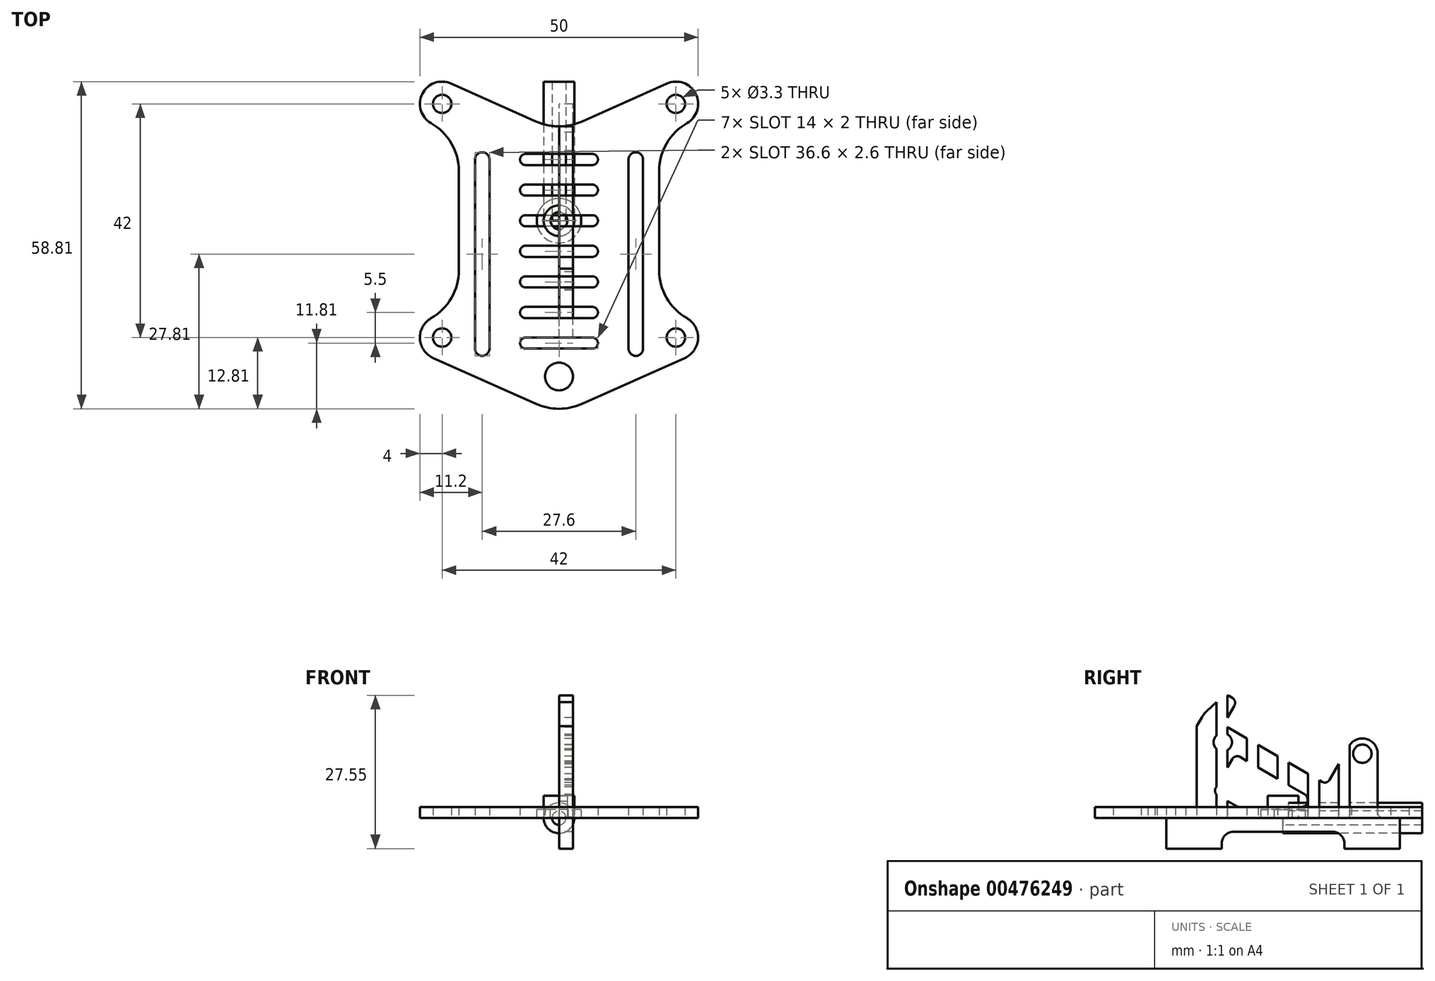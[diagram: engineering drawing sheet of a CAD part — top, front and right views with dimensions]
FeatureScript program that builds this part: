
annotation { "Feature Type Name" : "Feature", "Feature Type Description" : "" }
export const myFeature = defineFeature(function(context is Context, id is Id, definition is map)
    precondition{}
    {
        {
            var Q0;
            Q0=qCreatedBy(makeId("Right.planeOp"),FACE);
            var sketch = newSketch(context, id + "F0", { "sketchPlane" : qUnion([Q0])});
            skLineSegment(sketch, "E0.bottom", {"start": v(-21, 0) * mm, "end": v(-18, 0) * mm});
            skLineSegment(sketch, "E0.top", {"start": v(-21, -5.5) * mm, "end": v(-11, -5.5) * mm});
            skLineSegment(sketch, "E0.left", {"start": v(-21, 0) * mm, "end": v(-21, -5.5) * mm});
            skLineSegment(sketch, "E0.right", {"start": v(21, 0) * mm, "end": v(21, -5.5) * mm});
            skLineSegment(sketch, "E1.bottom", {"start": v(-9.89, 16.25) * mm, "end": v(7, 6.5) * mm});
            skLineSegment(sketch, "E1.left", {"start": v(-10.25, 17.62) * mm, "end": v(-8.75, 20.21) * mm});
            skPoint(sketch, "E1.middle", {"position": v(-0.2, 13.54) * mm});
            skLineSegment(sketch, "E2", {"start": v(8.37, 6.87) * mm, "end": v(11.87, 12.93) * mm});
            skLineSegment(sketch, "E3", {"start": v(17, 11.55) * mm, "end": v(17, 1) * mm});
            skLineSegment(sketch, "E4", {"start": v(-9.12, 21.58) * mm, "end": v(-9.77, 21.96) * mm});
            skLineSegment(sketch, "E5", {"start": v(-10.96, 21.82) * mm, "end": v(-13.68, 19.25) * mm});
            skLineSegment(sketch, "E6", {"start": v(-14.58, 18.11) * mm, "end": v(-16.33, 15.09) * mm});
            skLineSegment(sketch, "E7", {"start": v(-17, 12.59) * mm, "end": v(-17, 1) * mm});
            skArc(sketch, "E8", {"start": v(17, 11.55) * mm, "mid": v(14.96, 14.2) * mm, "end": v(11.87, 12.93) * mm});
            skLineSegment(sketch, "E9", {"start": v(-7.74, 10.97) * mm, "end": v(3.89, 4.26) * mm});
            skLineSegment(sketch, "E10", {"start": v(-7.94, 2) * mm, "end": v(3.39, 2) * mm});
            skLineSegment(sketch, "E11", {"start": v(-8.44, 2.13) * mm, "end": v(-11.74, 4.04) * mm});
            skLineSegment(sketch, "E12", {"start": v(-12.1, 5.4) * mm, "end": v(-9.1, 10.6) * mm});
            skLineSegment(sketch, "E13", {"start": v(4.39, 3.4) * mm, "end": v(4.39, 3) * mm});
            skLineSegment(sketch, "E14.trimOffspring", {"start": v(18, 0) * mm, "end": v(21, 0) * mm});
            skCircle(sketch, "E15", {"center": v(-10.83, 13.62) * mm, "radius": 1.65 * mm});
            skCircle(sketch, "E16", {"center": v(-10.83, 13.62) * mm, "radius": 2.75 * mm, "construction": true});
            skPoint(sketch, "E17.visualSharp", {"position": v(-8.6, 11.47) * mm});
            skArc(sketch, "E17.filletArc", {"start": v(-7.74, 10.97) * mm, "mid": v(-8.5, 11.07) * mm, "end": v(-9.1, 10.6) * mm});
            skPoint(sketch, "E18.visualSharp", {"position": v(4.39, 3.97) * mm});
            skArc(sketch, "E18.filletArc", {"start": v(4.39, 3.4) * mm, "mid": v(4.25, 3.9) * mm, "end": v(3.89, 4.26) * mm});
            skPoint(sketch, "E19.visualSharp", {"position": v(4.39, 2) * mm});
            skArc(sketch, "E19.filletArc", {"start": v(3.39, 2) * mm, "mid": v(4.1, 2.3) * mm, "end": v(4.39, 3) * mm});
            skPoint(sketch, "E20.visualSharp", {"position": v(-8.2, 2) * mm});
            skArc(sketch, "E20.filletArc", {"start": v(-8.44, 2.13) * mm, "mid": v(-8.2, 2.03) * mm, "end": v(-7.94, 2) * mm});
            skPoint(sketch, "E21.visualSharp", {"position": v(-12.6, 4.54) * mm});
            skArc(sketch, "E21.filletArc", {"start": v(-12.1, 5.4) * mm, "mid": v(-12.2, 4.65) * mm, "end": v(-11.74, 4.04) * mm});
            skPoint(sketch, "E22.visualSharp", {"position": v(17, 0) * mm});
            skArc(sketch, "E22.filletArc", {"start": v(17, 1) * mm, "mid": v(17.3, 0.3) * mm, "end": v(18, 0) * mm});
            skPoint(sketch, "E23.visualSharp", {"position": v(-17, 0) * mm});
            skArc(sketch, "E23.filletArc", {"start": v(-18, 0) * mm, "mid": v(-17.3, 0.3) * mm, "end": v(-17, 1) * mm});
            skPoint(sketch, "E24.visualSharp", {"position": v(-17, 13.93) * mm});
            skArc(sketch, "E24.filletArc", {"start": v(-16.33, 15.09) * mm, "mid": v(-16.83, 13.88) * mm, "end": v(-17, 12.59) * mm});
            skPoint(sketch, "E25.visualSharp", {"position": v(-14.22, 18.75) * mm});
            skArc(sketch, "E25.filletArc", {"start": v(-13.68, 19.25) * mm, "mid": v(-14.17, 18.72) * mm, "end": v(-14.58, 18.11) * mm});
            skPoint(sketch, "E26.visualSharp", {"position": v(-10.42, 22.33) * mm});
            skArc(sketch, "E26.filletArc", {"start": v(-9.77, 21.96) * mm, "mid": v(-10.39, 22.09) * mm, "end": v(-10.96, 21.82) * mm});
            skPoint(sketch, "E27.visualSharp", {"position": v(-8.25, 21.08) * mm});
            skArc(sketch, "E27.filletArc", {"start": v(-8.75, 20.21) * mm, "mid": v(-8.65, 20.97) * mm, "end": v(-9.12, 21.58) * mm});
            skPoint(sketch, "E28.visualSharp", {"position": v(-10.75, 16.75) * mm});
            skArc(sketch, "E28.filletArc", {"start": v(-10.25, 17.62) * mm, "mid": v(-10.35, 16.86) * mm, "end": v(-9.89, 16.25) * mm});
            skPoint(sketch, "E29.visualSharp", {"position": v(7.87, 6) * mm});
            skArc(sketch, "E29.filletArc", {"start": v(7, 6.5) * mm, "mid": v(7.76, 6.4) * mm, "end": v(8.37, 6.87) * mm});
            skCircle(sketch, "E30", {"center": v(14.25, 11.55) * mm, "radius": 1.65 * mm});
            skLineSegment(sketch, "E31", {"start": v(-11, -5.5) * mm, "end": v(-11, -4.5) * mm});
            skLineSegment(sketch, "E32", {"start": v(-9, -2.5) * mm, "end": v(9, -2.5) * mm});
            skLineSegment(sketch, "E33", {"start": v(11, -4.5) * mm, "end": v(11, -5.5) * mm});
            skLineSegment(sketch, "E34.trimOffspring", {"start": v(11, -5.5) * mm, "end": v(21, -5.5) * mm});
            skPoint(sketch, "E35.visualSharp", {"position": v(-11, -2.5) * mm});
            skArc(sketch, "E35.filletArc", {"start": v(-9, -2.5) * mm, "mid": v(-10.41, -3.09) * mm, "end": v(-11, -4.5) * mm});
            skPoint(sketch, "E36.visualSharp", {"position": v(11, -2.5) * mm});
            skArc(sketch, "E36.filletArc", {"start": v(11, -4.5) * mm, "mid": v(10.41, -3.09) * mm, "end": v(9, -2.5) * mm});
            skSolve(sketch);
        }
        {
            var Q0;
            Q0=makeQuery(id+"F0.imprint","IMPRINT",FACE,{"disambiguationData":[TD([[makeQuery(id+"F0.imprint","IMPRINT",EDGE,{"derivedFrom":sQuery(id+"F0.wireOp",EDGE,"E0.bottom")}),-1.0]])]});
            extrude(context, id + "F1", {"entities" : qUnion([Q0]), "depth" : 2.5 * mm, "offsetDistance" : 25 * mm});
        }
        {
            var Q0;
            Q0=qCreatedBy(makeId("Top.planeOp"),FACE);
            var sketch = newSketch(context, id + "F2", { "sketchPlane" : qUnion([Q0])});
            skCircle(sketch, "E37", {"center": v(-21, 21) * mm, "radius": 1.65 * mm});
            skCircle(sketch, "E38.MirrorC", {"center": v(21, 21) * mm, "radius": 1.65 * mm});
            skCircle(sketch, "E39.MirrorC", {"center": v(-21, -21) * mm, "radius": 1.65 * mm});
            skCircle(sketch, "E40.MirrorC", {"center": v(21, -21) * mm, "radius": 1.65 * mm});
            skArc(sketch, "E41", {"start": v(-19.37, 24.65) * mm, "mid": v(-24.56, 22.82) * mm, "end": v(-23, 17.54) * mm});
            skArc(sketch, "E42", {"start": v(-23, -17.54) * mm, "mid": v(-25, -21.2) * mm, "end": v(-22.63, -24.65) * mm});
            skArc(sketch, "E43", {"start": v(23, 17.54) * mm, "mid": v(24.56, 22.82) * mm, "end": v(19.37, 24.65) * mm});
            skArc(sketch, "E44", {"start": v(22.63, -24.65) * mm, "mid": v(25, -21.2) * mm, "end": v(23, -17.54) * mm});
            skLineSegment(sketch, "E45", {"start": v(-18, 8.88) * mm, "end": v(-18, -8.88) * mm});
            skLineSegment(sketch, "E46", {"start": v(18, 8.88) * mm, "end": v(18, -8.88) * mm});
            skArc(sketch, "E47", {"start": v(-18, 8.88) * mm, "mid": v(-19.34, 13.88) * mm, "end": v(-23, 17.54) * mm});
            skArc(sketch, "E48", {"start": v(-23, -17.54) * mm, "mid": v(-19.34, -13.88) * mm, "end": v(-18, -8.88) * mm});
            skArc(sketch, "E49", {"start": v(18, -8.88) * mm, "mid": v(19.34, -13.88) * mm, "end": v(23, -17.54) * mm});
            skArc(sketch, "E50", {"start": v(23, 17.54) * mm, "mid": v(19.34, 13.88) * mm, "end": v(18, 8.88) * mm});
            skLineSegment(sketch, "E51", {"start": v(-13.8, 11) * mm, "end": v(-13.8, -23) * mm, "construction": true});
            skArc(sketch, "E52.0.startCap", {"start": v(-15.1, 11) * mm, "mid": v(-13.8, 12.3) * mm, "end": v(-12.5, 11) * mm});
            skArc(sketch, "E52.0.endCap", {"start": v(-12.5, -23) * mm, "mid": v(-13.8, -24.3) * mm, "end": v(-15.1, -23) * mm});
            skLineSegment(sketch, "E52.0.left", {"start": v(-12.5, 11) * mm, "end": v(-12.5, -23) * mm});
            skLineSegment(sketch, "E52.0.right", {"start": v(-15.1, 11) * mm, "end": v(-15.1, -23) * mm});
            skArc(sketch, "E53.MirrorCS", {"start": v(15.1, 11) * mm, "mid": v(13.8, 12.3) * mm, "end": v(12.5, 11) * mm});
            skLineSegment(sketch, "E54.MirrorCS", {"start": v(15.1, 11) * mm, "end": v(15.1, -23) * mm});
            skArc(sketch, "E55.MirrorCS", {"start": v(12.5, -23) * mm, "mid": v(13.8, -24.3) * mm, "end": v(15.1, -23) * mm});
            skLineSegment(sketch, "E56.MirrorCS", {"start": v(13.8, 11) * mm, "end": v(13.8, -23) * mm, "construction": true});
            skLineSegment(sketch, "E57.MirrorCS", {"start": v(12.5, 11) * mm, "end": v(12.5, -23) * mm});
            skLineSegment(sketch, "E58", {"start": v(-19.37, 24.65) * mm, "end": v(-4.08, 17.82) * mm});
            skLineSegment(sketch, "E59", {"start": v(4.08, 17.82) * mm, "end": v(19.37, 24.65) * mm});
            skPoint(sketch, "E60.visualSharp", {"position": v(0, 16) * mm});
            skArc(sketch, "E60.filletArc", {"start": v(-4.08, 17.82) * mm, "mid": v(0, 16.95) * mm, "end": v(4.08, 17.82) * mm});
            skLineSegment(sketch, "E61", {"start": v(-22.63, -24.65) * mm, "end": v(-4.08, -32.94) * mm});
            skLineSegment(sketch, "E62", {"start": v(4.08, -32.94) * mm, "end": v(22.63, -24.65) * mm});
            skPoint(sketch, "E63.visualSharp", {"position": v(0, -34.76) * mm});
            skArc(sketch, "E63.filletArc", {"start": v(-4.08, -32.94) * mm, "mid": v(0, -33.8) * mm, "end": v(4.08, -32.94) * mm});
            skSolve(sketch);
        }
        {
            var Q0;
            Q0=makeQuery(id+"F2.imprint","IMPRINT",FACE,{"disambiguationData":[TD([[makeQuery(id+"F2.imprint","IMPRINT",EDGE,{"derivedFrom":sQuery(id+"F2.wireOp",EDGE,"E37")}),-1.0]])]});
            extrude(context, id + "F3", {"entities" : qUnion([Q0]), "depth" : 2 * mm, "offsetDistance" : 25 * mm});
        }
        {
            var Q0;
            Q0=qCreatedBy(makeId("Top.planeOp"),FACE);
            var sketch = newSketch(context, id + "F4", { "sketchPlane" : qUnion([Q0])});
            skLineSegment(sketch, "E64", {"start": v(0, 0) * mm, "end": v(0, 25) * mm, "construction": true});
            skLineSegment(sketch, "E65", {"start": v(1.25, 25) * mm, "end": v(2.75, 25) * mm});
            skLineSegment(sketch, "E66", {"start": v(2.75, 25) * mm, "end": v(2.75, 0) * mm});
            skLineSegment(sketch, "E67", {"start": v(2.75, 0) * mm, "end": v(1.25, 0) * mm});
            skLineSegment(sketch, "E68", {"start": v(1.25, 25) * mm, "end": v(1.25, 0) * mm});
            skSolve(sketch);
        }
        {
            var Q0;
            Q0=makeQuery(id+"F4.imprint","IMPRINT",FACE,{"disambiguationData":[TD([[makeQuery(id+"F4.imprint","IMPRINT",EDGE,{"derivedFrom":sQuery(id+"F4.wireOp",EDGE,"E65")}),-1.0]])]});
            var Q1;
            Q1=sQuery(id+"F4.wireOp",EDGE,"E64");
            revolve(context, id + "F5", {"entities" : qUnion([Q0]), "axis" : qUnion([Q1]), "revolveType" : RevolveType.FULL});
        }
        {
            var Q0;
            Q0=makeQuery(id+"F3.opExtrude","CAP_FACE",FACE,{"disambiguationData":[OSD([sQuery(id+"F2.wireOp",EDGE,"E37"),sQuery(id+"F2.wireOp",EDGE,"E38.MirrorC"),sQuery(id+"F2.wireOp",EDGE,"E39.MirrorC"),sQuery(id+"F2.wireOp",EDGE,"E40.MirrorC"),sQuery(id+"F2.wireOp",EDGE,"E41"),sQuery(id+"F2.wireOp",EDGE,"E42"),sQuery(id+"F2.wireOp",EDGE,"E43"),sQuery(id+"F2.wireOp",EDGE,"E44"),sQuery(id+"F2.wireOp",EDGE,"HbRvRGti-VTHd-3TSI-MkX5-C2cFPtapRuhi"),sQuery(id+"F2.wireOp",EDGE,"Mz0DYlBK-cip7-vn1s-uTGy-A6edBpfErfw1"),sQuery(id+"F2.wireOp",EDGE,"E45"),sQuery(id+"F2.wireOp",EDGE,"E46"),sQuery(id+"F2.wireOp",EDGE,"E47"),sQuery(id+"F2.wireOp",EDGE,"E48"),sQuery(id+"F2.wireOp",EDGE,"E49"),sQuery(id+"F2.wireOp",EDGE,"E50"),sQuery(id+"F2.wireOp",EDGE,"E52.0.startCap"),sQuery(id+"F2.wireOp",EDGE,"E52.0.endCap"),sQuery(id+"F2.wireOp",EDGE,"E52.0.left"),sQuery(id+"F2.wireOp",EDGE,"E52.0.right"),sQuery(id+"F2.wireOp",EDGE,"E53.MirrorCS"),sQuery(id+"F2.wireOp",EDGE,"E54.MirrorCS"),sQuery(id+"F2.wireOp",EDGE,"E55.MirrorCS"),sQuery(id+"F2.wireOp",EDGE,"E57.MirrorCS")])],"isStart":true});
            var sketch = newSketch(context, id + "F6", { "sketchPlane" : qUnion([Q0])});
            skLineSegment(sketch, "E69", {"start": v(-6, 22) * mm, "end": v(6, 22) * mm, "construction": true});
            skArc(sketch, "E70.0.startCap", {"start": v(-6, 21) * mm, "mid": v(-7, 22) * mm, "end": v(-6, 23) * mm});
            skArc(sketch, "E70.0.endCap", {"start": v(6, 23) * mm, "mid": v(7, 22) * mm, "end": v(6, 21) * mm});
            skLineSegment(sketch, "E70.0.left", {"start": v(-6, 23) * mm, "end": v(6, 23) * mm});
            skLineSegment(sketch, "E70.0.right", {"start": v(-6, 21) * mm, "end": v(6, 21) * mm});
            skArc(sketch, "E71.0.1.0", {"start": v(-6, 15.5) * mm, "mid": v(-7, 16.5) * mm, "end": v(-6, 17.5) * mm});
            skArc(sketch, "E71.0.1.1", {"start": v(6, 17.5) * mm, "mid": v(7, 16.5) * mm, "end": v(6, 15.5) * mm});
            skLineSegment(sketch, "E71.0.1.2", {"start": v(-6, 15.5) * mm, "end": v(6, 15.5) * mm});
            skLineSegment(sketch, "E71.0.1.3", {"start": v(-6, 17.5) * mm, "end": v(6, 17.5) * mm});
            skLineSegment(sketch, "E71.0.1.4", {"start": v(-6, 16.5) * mm, "end": v(6, 16.5) * mm, "construction": true});
            skArc(sketch, "E71.0.2.0", {"start": v(-6, 10) * mm, "mid": v(-7, 11) * mm, "end": v(-6, 12) * mm});
            skArc(sketch, "E71.0.2.1", {"start": v(6, 12) * mm, "mid": v(7, 11) * mm, "end": v(6, 10) * mm});
            skLineSegment(sketch, "E71.0.2.2", {"start": v(-6, 10) * mm, "end": v(6, 10) * mm});
            skLineSegment(sketch, "E71.0.2.3", {"start": v(-6, 12) * mm, "end": v(6, 12) * mm});
            skLineSegment(sketch, "E71.0.2.4", {"start": v(-6, 11) * mm, "end": v(6, 11) * mm, "construction": true});
            skArc(sketch, "E71.0.3.0", {"start": v(-6, 4.5) * mm, "mid": v(-7, 5.5) * mm, "end": v(-6, 6.5) * mm});
            skArc(sketch, "E71.0.3.1", {"start": v(6, 6.5) * mm, "mid": v(7, 5.5) * mm, "end": v(6, 4.5) * mm});
            skLineSegment(sketch, "E71.0.3.2", {"start": v(-6, 4.5) * mm, "end": v(6, 4.5) * mm});
            skLineSegment(sketch, "E71.0.3.3", {"start": v(-6, 6.5) * mm, "end": v(6, 6.5) * mm});
            skLineSegment(sketch, "E71.0.3.4", {"start": v(-6, 5.5) * mm, "end": v(6, 5.5) * mm, "construction": true});
            skArc(sketch, "E71.0.4.0", {"start": v(-6, -1) * mm, "mid": v(-7, 0) * mm, "end": v(-6, 1) * mm});
            skArc(sketch, "E71.0.4.1", {"start": v(6, 1) * mm, "mid": v(7, 0) * mm, "end": v(6, -1) * mm});
            skLineSegment(sketch, "E71.0.4.2", {"start": v(-6, -1) * mm, "end": v(6, -1) * mm});
            skLineSegment(sketch, "E71.0.4.3", {"start": v(-6, 1) * mm, "end": v(6, 1) * mm});
            skLineSegment(sketch, "E71.0.4.4", {"start": v(-6, 0) * mm, "end": v(6, 0) * mm, "construction": true});
            skArc(sketch, "E71.0.5.0", {"start": v(-6, -6.5) * mm, "mid": v(-7, -5.5) * mm, "end": v(-6, -4.5) * mm});
            skArc(sketch, "E71.0.5.1", {"start": v(6, -4.5) * mm, "mid": v(7, -5.5) * mm, "end": v(6, -6.5) * mm});
            skLineSegment(sketch, "E71.0.5.2", {"start": v(-6, -6.5) * mm, "end": v(6, -6.5) * mm});
            skLineSegment(sketch, "E71.0.5.3", {"start": v(-6, -4.5) * mm, "end": v(6, -4.5) * mm});
            skLineSegment(sketch, "E71.0.5.4", {"start": v(-6, -5.5) * mm, "end": v(6, -5.5) * mm, "construction": true});
            skArc(sketch, "E71.0.6.0", {"start": v(-6, -12) * mm, "mid": v(-7, -11) * mm, "end": v(-6, -10) * mm});
            skArc(sketch, "E71.0.6.1", {"start": v(6, -10) * mm, "mid": v(7, -11) * mm, "end": v(6, -12) * mm});
            skLineSegment(sketch, "E71.0.6.2", {"start": v(-6, -12) * mm, "end": v(6, -12) * mm});
            skLineSegment(sketch, "E71.0.6.3", {"start": v(-6, -10) * mm, "end": v(6, -10) * mm});
            skLineSegment(sketch, "E71.0.6.4", {"start": v(-6, -11) * mm, "end": v(6, -11) * mm, "construction": true});
            skLineSegment(sketch, "E71.direction1", {"start": v(-6, 21) * mm, "end": v(19, 21) * mm, "construction": true});
            skLineSegment(sketch, "E71.direction2", {"start": v(-6, 21) * mm, "end": v(-6, 15.5) * mm, "construction": true});
            skCircle(sketch, "E72", {"center": v(0, 28) * mm, "radius": 2.5 * mm});
            skSolve(sketch);
        }
        {
            var Q0;
            Q0 = qSketchRegion(id + "F6", true);
            extrude(context, id + "F7", {"entities" : qUnion([Q0]), "operationType" : NewBodyOperationType.REMOVE, "oppositeDirection" : true, "depth" : 25 * mm, "offsetDistance" : 25 * mm});
        }
        {
            var Q0;
            Q0=qCreatedBy(makeId("Top.planeOp"),FACE);
            var sketch = newSketch(context, id + "F8", { "sketchPlane" : qUnion([Q0])});
            skCircle(sketch, "E73", {"center": v(0, 0) * mm, "radius": 2.75 * mm});
            skCircle(sketch, "E74", {"center": v(0, 0) * mm, "radius": 1.5 * mm});
            skSolve(sketch);
        }
        {
            var Q0;
            Q0=makeQuery(id+"F8.imprint","IMPRINT",FACE,{"disambiguationData":[TD([[makeQuery(id+"F8.imprint","IMPRINT",EDGE,{"derivedFrom":sQuery(id+"F8.wireOp",EDGE,"E73")}),1.0]])]});
            extrude(context, id + "F9", {"entities" : qUnion([Q0]), "depth" : 4 * mm, "offsetDistance" : 25 * mm});
        }
        {
            var Q0;
            Q0=qCreatedBy(makeId("Top.planeOp"),FACE);
            var sketch = newSketch(context, id + "F10", { "sketchPlane" : qUnion([Q0])});
            skCircle(sketch, "E75", {"center": v(0, 0) * mm, "radius": 4 * mm});
            skCircle(sketch, "E76", {"center": v(0, 0) * mm, "radius": 1.65 * mm});
            skSolve(sketch);
        }
        {
            var Q0;
            Q0=makeQuery(id+"F10.imprint","IMPRINT",FACE,{"disambiguationData":[TD([[makeQuery(id+"F10.imprint","IMPRINT",EDGE,{"derivedFrom":sQuery(id+"F10.wireOp",EDGE,"E75")}),1.0]])]});
            extrude(context, id + "F11", {"entities" : qUnion([Q0]), "depth" : 1.5 * mm, "offsetDistance" : 25 * mm});
        }
    });
